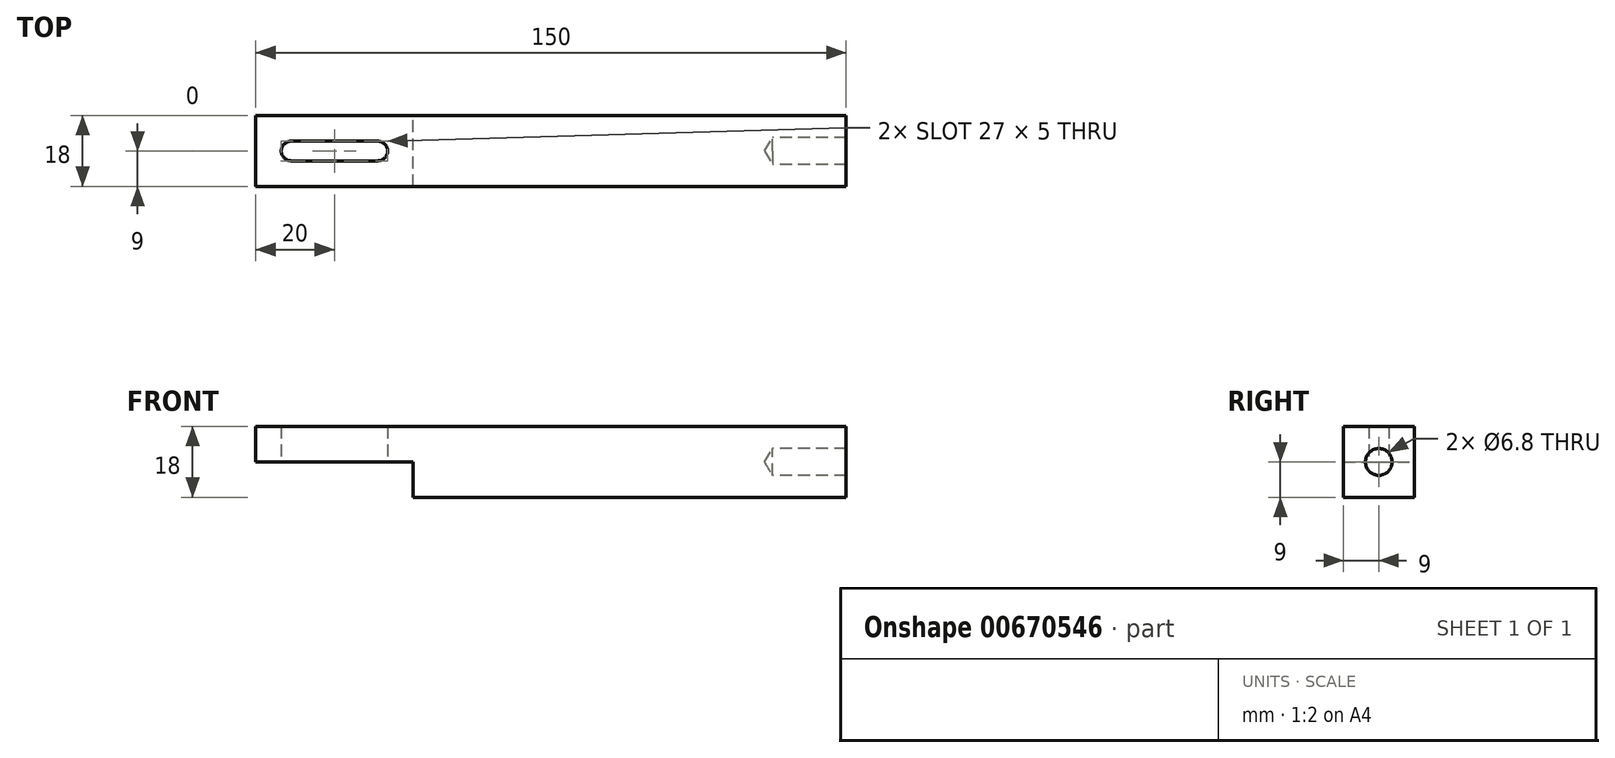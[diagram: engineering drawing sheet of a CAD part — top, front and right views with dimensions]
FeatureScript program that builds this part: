
annotation { "Feature Type Name" : "Feature", "Feature Type Description" : "" }
export const myFeature = defineFeature(function(context is Context, id is Id, definition is map)
    precondition{}
    {
        {
            var Q0;
            Q0=qCreatedBy(makeId("Right.planeOp"),FACE);
            var sketch = newSketch(context, id + "F0", { "sketchPlane" : qUnion([Q0])});
            skLineSegment(sketch, "E0.bottom", {"start": v(-9, 9) * mm, "end": v(9, 9) * mm});
            skLineSegment(sketch, "E0.top", {"start": v(-9, -9) * mm, "end": v(9, -9) * mm});
            skLineSegment(sketch, "E0.left", {"start": v(-9, 9) * mm, "end": v(-9, -9) * mm});
            skLineSegment(sketch, "E0.right", {"start": v(9, 9) * mm, "end": v(9, -9) * mm});
            skSolve(sketch);
        }
        {
            var Q0;
            Q0=makeQuery(id+"F0.imprint","IMPRINT",FACE,{"disambiguationData":[TD([[makeQuery(id+"F0.imprint","IMPRINT",EDGE,{"derivedFrom":sQuery(id+"F0.wireOp",EDGE,"E0.bottom")}),-1.0]])]});
            extrude(context, id + "F1", {"entities" : qUnion([Q0]), "depth" : 150 * mm, "offsetDistance" : 25 * mm});
        }
        {
            var Q0;
            Q0=makeQuery(id+"F1.opExtrude","SWEPT_FACE",FACE,{"disambiguationData":[OSD([sQuery(id+"F0.wireOp",EDGE,"E0.top")])]});
            var sketch = newSketch(context, id + "F2", { "sketchPlane" : qUnion([Q0])});
            skLineSegment(sketch, "E1.bottom", {"start": v(0, 9) * mm, "end": v(40, 9) * mm});
            skLineSegment(sketch, "E1.top", {"start": v(0, -9) * mm, "end": v(40, -9) * mm});
            skLineSegment(sketch, "E1.left", {"start": v(0, 9) * mm, "end": v(0, -9) * mm});
            skLineSegment(sketch, "E1.right", {"start": v(40, 9) * mm, "end": v(40, -9) * mm});
            skPoint(sketch, "E2", {"position": v(31, 0) * mm});
            skPoint(sketch, "E3", {"position": v(9, 0) * mm});
            skCircle(sketch, "E4", {"center": v(9, 0) * mm, "radius": 2.5 * mm});
            skCircle(sketch, "E5", {"center": v(31, 0) * mm, "radius": 2.5 * mm});
            skLineSegment(sketch, "E6.bottom", {"start": v(9, 2.5) * mm, "end": v(31, 2.5) * mm});
            skLineSegment(sketch, "E6.top", {"start": v(9, -2.5) * mm, "end": v(31, -2.5) * mm});
            skLineSegment(sketch, "E6.left", {"start": v(9, 2.5) * mm, "end": v(9, -2.5) * mm});
            skLineSegment(sketch, "E6.right", {"start": v(31, 2.5) * mm, "end": v(31, -2.5) * mm});
            skSolve(sketch);
        }
        {
            var Q0;
            Q0=makeQuery(id+"F2.imprint","IMPRINT",FACE,{"disambiguationData":[TD([[makeQuery(id+"F2.imprint","IMPRINT",EDGE,{"derivedFrom":sQuery(id+"F2.wireOp",EDGE,"E1.bottom")}),1.0]])]});
            extrude(context, id + "F3", {"entities" : qUnion([Q0]), "operationType" : NewBodyOperationType.REMOVE, "oppositeDirection" : true, "depth" : 9 * mm, "offsetDistance" : 25 * mm});
        }
        {
            var Q0;
            Q0=makeQuery(id+"F3.boolean.opBoolean","SPLIT",FACE,{"disambiguationData":[TD([makeQuery(id+"F3.opExtrude","SWEPT_FACE",FACE,{"disambiguationData":[OSD([sQuery(id+"F2.wireOp",EDGE,"E4")])]})])],"derivedFrom":makeQuery(id+"F1.opExtrude","SWEPT_FACE",FACE,{"disambiguationData":[OSD([sQuery(id+"F0.wireOp",EDGE,"E0.top")])]})});
            extrude(context, id + "F4", {"entities" : qUnion([Q0]), "operationType" : NewBodyOperationType.REMOVE, "oppositeDirection" : true, "depth" : 25 * mm, "offsetDistance" : 25 * mm});
        }
        {
            var Q0;
            Q0=makeQuery(id+"F1.opExtrude","CAP_FACE",FACE,{"disambiguationData":[OSD([sQuery(id+"F0.wireOp",EDGE,"E0.bottom"),sQuery(id+"F0.wireOp",EDGE,"E0.top"),sQuery(id+"F0.wireOp",EDGE,"E0.left"),sQuery(id+"F0.wireOp",EDGE,"E0.right")])],"isStart":false});
            var sketch = newSketch(context, id + "F5", { "sketchPlane" : qUnion([Q0])});
            skPoint(sketch, "E7", {"position": v(0, 0) * mm});
            skSolve(sketch);
        }
        {
            var Q0;
            Q0=sQuery(id+"F5.wireOp",VERTEX,"E7");
            var Q1;
            Q1=makeQuery(id+"F1.opExtrude","SWEPT_BODY",BODY,{"disambiguationData":[OSD([sQuery(id+"F0.wireOp",EDGE,"E0.bottom"),sQuery(id+"F0.wireOp",EDGE,"E0.top"),sQuery(id+"F0.wireOp",EDGE,"E0.left"),sQuery(id+"F0.wireOp",EDGE,"E0.right")])]});
            hole(context, id + "F6", {"style" : HoleStyle.SIMPLE, "endStyle" : HoleEndStyle.BLIND, "standardTappedOrClearance" : lookupTablePath({ "standard" : "ISO", "engagement" : "75%", "pitch" : "1.25 mm", "size" : "M8", "type" : "Tapped" }), "standardBlindInLast" : lookupTablePath({ "standard" : "ISO", "engagement" : "75%", "pitch" : "1.25 mm", "size" : "M8", "type" : "Tapped" }), "holeDiameter" : 6.8 * mm, "majorDiameter" : 8 * mm, "showTappedDepth" : true, "holeDepth" : 18.75 * mm, "isTappedThrough" : true, "tappedDepth" : 15 * mm, "tapClearance" : 3, "locations" : qUnion([Q0]), "scope" : qUnion([Q1]), "startStyle" : HoleStartStyle.PART});
        }
    });
